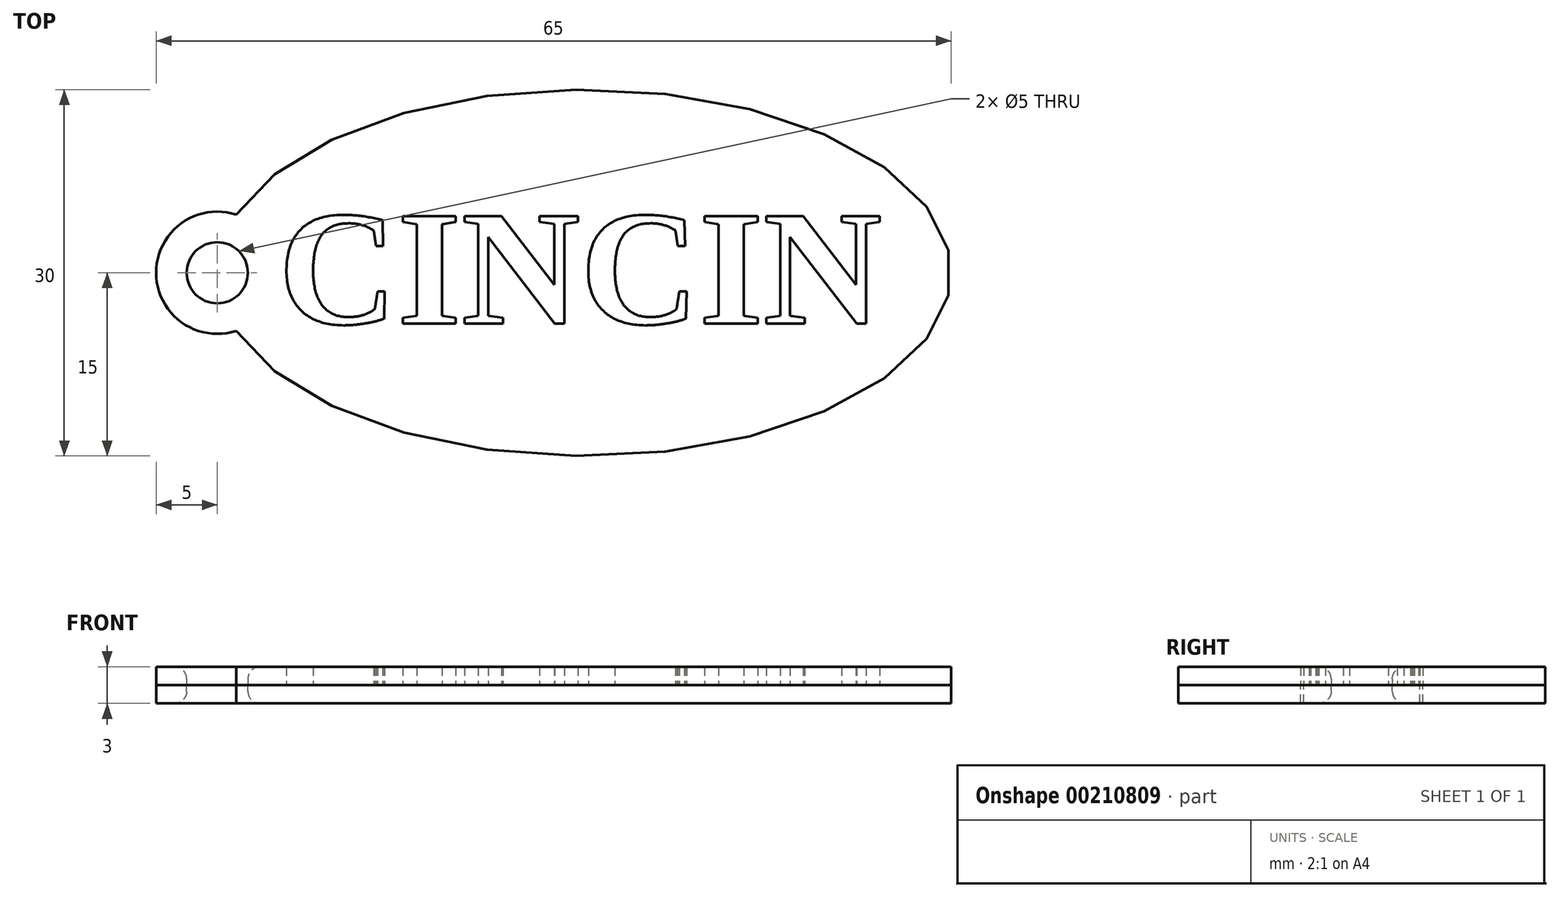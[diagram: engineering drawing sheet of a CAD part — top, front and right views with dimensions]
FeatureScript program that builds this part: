
annotation { "Feature Type Name" : "Feature", "Feature Type Description" : "" }
export const myFeature = defineFeature(function(context is Context, id is Id, definition is map)
    precondition{}
    {
        {
            var Q0;
            Q0=qCreatedBy(makeId("Top.planeOp"),FACE);
            var sketch = newSketch(context, id + "F0", { "sketchPlane" : qUnion([Q0])});
            skEllipse(sketch, "E0", {"center": v(0, 0) * mm, "majorRadius": 30 * mm, "minorRadius": 15 * mm, "majorAxis": v(1, 0)});
            skCircle(sketch, "E1", {"center": v(-30, 0) * mm, "radius": 5 * mm});
            skFitSpline(sketch, "E2.0", {"points": [v(27.93, -1.1) * mm, v(28.04, 0) * mm, v(27.93, 1.1) * mm, v(27.6, 2.2) * mm, v(27.04, 3.32) * mm, v(26.22, 4.46) * mm, v(25.14, 5.6) * mm, v(23.8, 6.73) * mm, v(22.47, 7.63) * mm, v(21.28, 8.32) * mm, v(20.33, 8.82) * mm, v(19.32, 9.3) * mm, v(17.91, 9.9) * mm, v(16.04, 10.6) * mm, v(13.63, 11.32) * mm, v(11.1, 11.92) * mm, v(8.44, 12.4) * mm, v(5.7, 12.74) * mm, v(3.34, 12.92) * mm, v(1.44, 12.99) * mm, v(0, 13) * mm, v(-1.44, 12.99) * mm, v(-3.34, 12.92) * mm, v(-5.7, 12.74) * mm, v(-8.44, 12.4) * mm, v(-11.1, 11.92) * mm, v(-13.63, 11.32) * mm, v(-16.04, 10.6) * mm, v(-17.91, 9.9) * mm, v(-19.32, 9.3) * mm, v(-20.33, 8.82) * mm, v(-21.28, 8.32) * mm, v(-22.47, 7.63) * mm, v(-23.8, 6.73) * mm, v(-25.14, 5.6) * mm, v(-26.22, 4.46) * mm, v(-27.04, 3.32) * mm, v(-27.6, 2.2) * mm, v(-27.93, 1.1) * mm, v(-28.04, 0) * mm, v(-27.93, -1.1) * mm, v(-27.6, -2.2) * mm, v(-27.04, -3.32) * mm, v(-26.22, -4.46) * mm, v(-25.14, -5.6) * mm, v(-23.8, -6.73) * mm, v(-22.47, -7.63) * mm, v(-21.28, -8.32) * mm, v(-20.33, -8.82) * mm, v(-19.32, -9.3) * mm, v(-17.91, -9.9) * mm, v(-16.04, -10.6) * mm, v(-13.63, -11.32) * mm, v(-11.1, -11.92) * mm, v(-8.44, -12.4) * mm, v(-5.7, -12.74) * mm, v(-3.34, -12.92) * mm, v(-1.44, -12.99) * mm, v(0, -13) * mm, v(1.44, -12.99) * mm, v(3.34, -12.92) * mm, v(5.7, -12.74) * mm, v(8.44, -12.4) * mm, v(11.1, -11.92) * mm, v(13.63, -11.32) * mm, v(16.04, -10.6) * mm, v(17.91, -9.9) * mm, v(19.32, -9.3) * mm, v(20.33, -8.82) * mm, v(21.28, -8.32) * mm, v(22.47, -7.63) * mm, v(23.8, -6.73) * mm, v(25.14, -5.6) * mm, v(26.22, -4.46) * mm, v(27.04, -3.32) * mm, v(27.6, -2.2) * mm, v(27.93, -1.1) * mm, v(28.04, 0) * mm, v(27.93, 1.1) * mm, v(27.93, -1.1) * mm]});
            skCircle(sketch, "E3", {"center": v(-30, 0) * mm, "radius": 2.5 * mm});
            skSolve(sketch);
        }
        {
            var Q0;
            Q0=qCreatedBy(makeId("Top.planeOp"),FACE);
            var sketch = newSketch(context, id + "F1", { "sketchPlane" : qUnion([Q0])});
            skText(sketch, "E4", { "text": "CINCIN", "fontName": "Tinos-Bold.ttf"});
            const initialGuessF1  = {"E4": [-0.025, -0.00417, 1, 0, 0.00969]};
            skSetInitialGuess(sketch, initialGuessF1);
            skSolve(sketch);
        }
        {
            var Q0;
            {var subQ0=sQuery(id+"F0.wireOp",EDGE,"E1");var subQ1=sQuery(id+"F0.wireOp",EDGE,"E0");var subQ2=makeQuery(id+"F0.imprint","INTERSECT",VERTEX,{"disambiguationData":[OD(0.0)],"derivedFrom":[subQ1,subQ0]});Q0=makeQuery(id+"F0.imprint","IMPRINT",FACE,{"disambiguationData":[TD([[makeQuery(id+"F0.imprint","IMPRINT",EDGE,{"disambiguationData":[TD([[subQ2,1.0]])],"derivedFrom":subQ1}),1.0]])]});}
            var Q1;
            {var subQ0=sQuery(id+"F0.wireOp",EDGE,"E2.0");var subQ1=sQuery(id+"F0.wireOp",EDGE,"E1");var subQ2=makeQuery(id+"F0.imprint","INTERSECT",VERTEX,{"disambiguationData":[OD(0.0)],"derivedFrom":[subQ1,subQ0]});Q1=makeQuery(id+"F0.imprint","IMPRINT",FACE,{"disambiguationData":[TD([[makeQuery(id+"F0.imprint","IMPRINT",EDGE,{"disambiguationData":[TD([[subQ2,1.0]])],"derivedFrom":subQ1}),-1.0]])]});}
            var Q2;
            {var subQ0=sQuery(id+"F0.wireOp",EDGE,"E2.0");var subQ1=sQuery(id+"F0.wireOp",EDGE,"E1");var subQ2=makeQuery(id+"F0.imprint","INTERSECT",VERTEX,{"disambiguationData":[OD(0.0)],"derivedFrom":[subQ1,subQ0]});Q2=makeQuery(id+"F0.imprint","IMPRINT",FACE,{"disambiguationData":[TD([[makeQuery(id+"F0.imprint","IMPRINT",EDGE,{"disambiguationData":[TD([[subQ2,1.0]])],"derivedFrom":subQ1}),1.0]])]});}
            var Q3;
            {var subQ0=sQuery(id+"F0.wireOp",EDGE,"E1");var subQ1=sQuery(id+"F0.wireOp",EDGE,"E0");var subQ2=makeQuery(id+"F0.imprint","INTERSECT",VERTEX,{"disambiguationData":[OD(0.0)],"derivedFrom":[subQ1,subQ0]});Q3=makeQuery(id+"F0.imprint","IMPRINT",FACE,{"disambiguationData":[TD([[makeQuery(id+"F0.imprint","IMPRINT",EDGE,{"disambiguationData":[TD([[subQ2,-1.0]])],"derivedFrom":subQ1}),-1.0]])]});}
            var Q4;
            {var subQ0=sQuery(id+"F0.wireOp",EDGE,"E1");var subQ1=sQuery(id+"F0.wireOp",EDGE,"E0");var subQ2=makeQuery(id+"F0.imprint","INTERSECT",VERTEX,{"disambiguationData":[OD(0.0)],"derivedFrom":[subQ1,subQ0]});Q4=makeQuery(id+"F0.imprint","IMPRINT",FACE,{"disambiguationData":[TD([[makeQuery(id+"F0.imprint","IMPRINT",EDGE,{"disambiguationData":[TD([[subQ2,-1.0]])],"derivedFrom":subQ1}),1.0]])]});}
            var Q5;
            {var subQ0=sQuery(id+"F0.wireOp",EDGE,"E1");var subQ1=sQuery(id+"F0.wireOp",EDGE,"E0");var subQ2=makeQuery(id+"F0.imprint","INTERSECT",VERTEX,{"disambiguationData":[OD(1.0)],"derivedFrom":[subQ1,subQ0]});Q5=makeQuery(id+"F0.imprint","IMPRINT",FACE,{"disambiguationData":[TD([[makeQuery(id+"F0.imprint","IMPRINT",EDGE,{"disambiguationData":[TD([[subQ2,1.0]])],"derivedFrom":subQ1}),1.0]])]});}
            extrude(context, id + "F2", {"entities" : qUnion([Q0, Q1, Q2, Q3, Q4, Q5]), "oppositeDirection" : true, "depth" : 1.5 * mm, "offsetDistance" : 25 * mm});
        }
        {
            var Q0;
            Q0 = qSketchRegion(id + "F1", true);
            var Q1;
            {var subQ0=sQuery(id+"F0.wireOp",EDGE,"E1");var subQ1=sQuery(id+"F0.wireOp",EDGE,"E0");var subQ2=makeQuery(id+"F0.imprint","INTERSECT",VERTEX,{"disambiguationData":[OD(0.0)],"derivedFrom":[subQ1,subQ0]});Q1=makeQuery(id+"F0.imprint","IMPRINT",FACE,{"disambiguationData":[TD([[makeQuery(id+"F0.imprint","IMPRINT",EDGE,{"disambiguationData":[TD([[subQ2,-1.0]])],"derivedFrom":subQ1}),-1.0]])]});}
            var Q2;
            {var subQ0=sQuery(id+"F0.wireOp",EDGE,"E1");var subQ1=sQuery(id+"F0.wireOp",EDGE,"E0");var subQ2=makeQuery(id+"F0.imprint","INTERSECT",VERTEX,{"disambiguationData":[OD(1.0)],"derivedFrom":[subQ1,subQ0]});Q2=makeQuery(id+"F0.imprint","IMPRINT",FACE,{"disambiguationData":[TD([[makeQuery(id+"F0.imprint","IMPRINT",EDGE,{"disambiguationData":[TD([[subQ2,1.0]])],"derivedFrom":subQ1}),1.0]])]});}
            var Q3;
            {var subQ0=sQuery(id+"F0.wireOp",EDGE,"E2.0");var subQ1=sQuery(id+"F0.wireOp",EDGE,"E1");var subQ2=makeQuery(id+"F0.imprint","INTERSECT",VERTEX,{"disambiguationData":[OD(0.0)],"derivedFrom":[subQ1,subQ0]});Q3=makeQuery(id+"F0.imprint","IMPRINT",FACE,{"disambiguationData":[TD([[makeQuery(id+"F0.imprint","IMPRINT",EDGE,{"disambiguationData":[TD([[subQ2,1.0]])],"derivedFrom":subQ1}),1.0]])]});}
            var Q4;
            {var subQ0=sQuery(id+"F0.wireOp",EDGE,"E1");var subQ1=sQuery(id+"F0.wireOp",EDGE,"E0");var subQ2=makeQuery(id+"F0.imprint","INTERSECT",VERTEX,{"disambiguationData":[OD(0.0)],"derivedFrom":[subQ1,subQ0]});Q4=makeQuery(id+"F0.imprint","IMPRINT",FACE,{"disambiguationData":[TD([[makeQuery(id+"F0.imprint","IMPRINT",EDGE,{"disambiguationData":[TD([[subQ2,1.0]])],"derivedFrom":subQ1}),1.0]])]});}
            var Q5;
            {var subQ0=sQuery(id+"F0.wireOp",EDGE,"E1");var subQ1=sQuery(id+"F0.wireOp",EDGE,"E0");var subQ2=makeQuery(id+"F0.imprint","INTERSECT",VERTEX,{"disambiguationData":[OD(0.0)],"derivedFrom":[subQ1,subQ0]});Q5=makeQuery(id+"F0.imprint","IMPRINT",FACE,{"disambiguationData":[TD([[makeQuery(id+"F0.imprint","IMPRINT",EDGE,{"disambiguationData":[TD([[subQ2,-1.0]])],"derivedFrom":subQ1}),1.0]])]});}
            extrude(context, id + "F3", {"entities" : qUnion([Q0, Q1, Q2, Q3, Q4, Q5]), "depth" : 1.5 * mm, "offsetDistance" : 25 * mm});
        }
        {
            var Q0;
            Q0=makeQuery(id+"F3.opExtrude","CAP_EDGE",EDGE,{"disambiguationData":[OSD([sQuery(id+"F0.wireOp",EDGE,"E3")])],"isStart":false});
            var Q1;
            Q1=makeQuery(id+"F2.opExtrude","CAP_EDGE",EDGE,{"disambiguationData":[OSD([sQuery(id+"F0.wireOp",EDGE,"E3")])],"isStart":false});
            fillet(context, id + "F4", {"entities" : qUnion([Q0, Q1]), "radius" : 1 * mm, "tangentPropagation" : true, "allowEdgeOverflow" : false});
        }
    });
